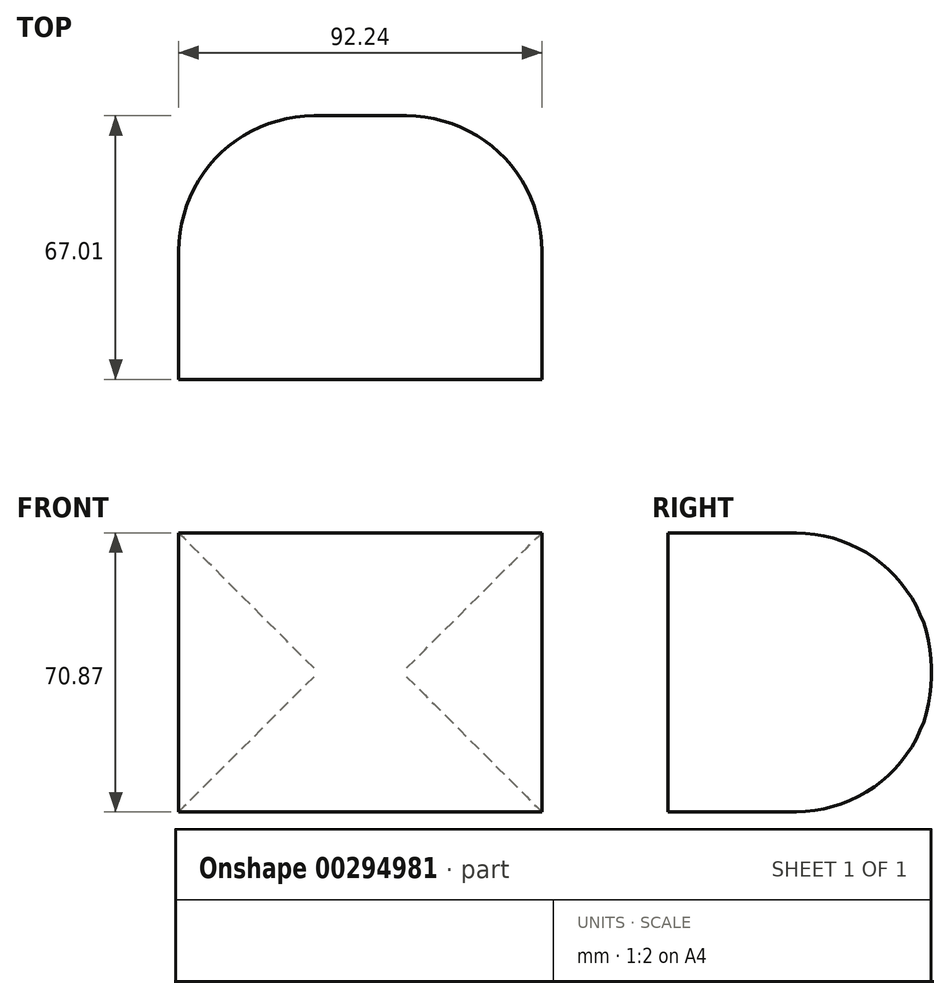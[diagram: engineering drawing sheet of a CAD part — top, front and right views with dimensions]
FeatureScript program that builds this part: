
annotation { "Feature Type Name" : "Feature", "Feature Type Description" : "" }
export const myFeature = defineFeature(function(context is Context, id is Id, definition is map)
    precondition{}
    {
        {
            var Q0;
            Q0=qCreatedBy(makeId("Top.planeOp"),FACE);
            var sketch = newSketch(context, id + "F0", { "sketchPlane" : qUnion([Q0])});
            skLineSegment(sketch, "E0.bottom", {"start": v(-51.88, 30.62) * mm, "end": v(-46.84, 30.62) * mm});
            skLineSegment(sketch, "E0.top", {"start": v(-51.88, 28.46) * mm, "end": v(-46.84, 28.46) * mm});
            skLineSegment(sketch, "E0.left", {"start": v(-51.88, 30.62) * mm, "end": v(-51.88, 28.46) * mm});
            skLineSegment(sketch, "E0.right", {"start": v(-46.84, 30.62) * mm, "end": v(-46.84, 28.46) * mm});
            skLineSegment(sketch, "E1.bottom", {"start": v(-46.84, 30.62) * mm, "end": v(45.4, 30.62) * mm});
            skLineSegment(sketch, "E1.top", {"start": v(-46.84, -36.39) * mm, "end": v(45.4, -36.39) * mm});
            skLineSegment(sketch, "E1.left", {"start": v(-46.84, 30.62) * mm, "end": v(-46.84, -36.39) * mm});
            skLineSegment(sketch, "E1.right", {"start": v(45.4, 30.62) * mm, "end": v(45.4, -36.39) * mm});
            skSolve(sketch);
        }
        {
            var Q0;
            {var subQ3=sQuery(id+"F0.wireOp",EDGE,"E1.bottom");Q0=makeQuery(id+"F0.imprint","IMPRINT",FACE,{"disambiguationData":[TD([[makeQuery(id+"F0.imprint","IMPRINT",EDGE,{"derivedFrom":subQ3}),-1.0]])]});}
            extrude(context, id + "F1", {"entities" : qUnion([Q0]), "depth" : 70.87 * mm});
        }
        {
            var Q0;
            Q0=makeQuery(id+"F1.opExtrude","SWEPT_FACE",FACE,{"disambiguationData":[OSD([sQuery(id+"F0.wireOp",EDGE,"E1.bottom")])]});
            fillet(context, id + "F2", {"entities" : qUnion([Q0]), "radius" : 34.34 * mm, "tangentPropagation" : true, "allowEdgeOverflow" : false});
        }
    });
